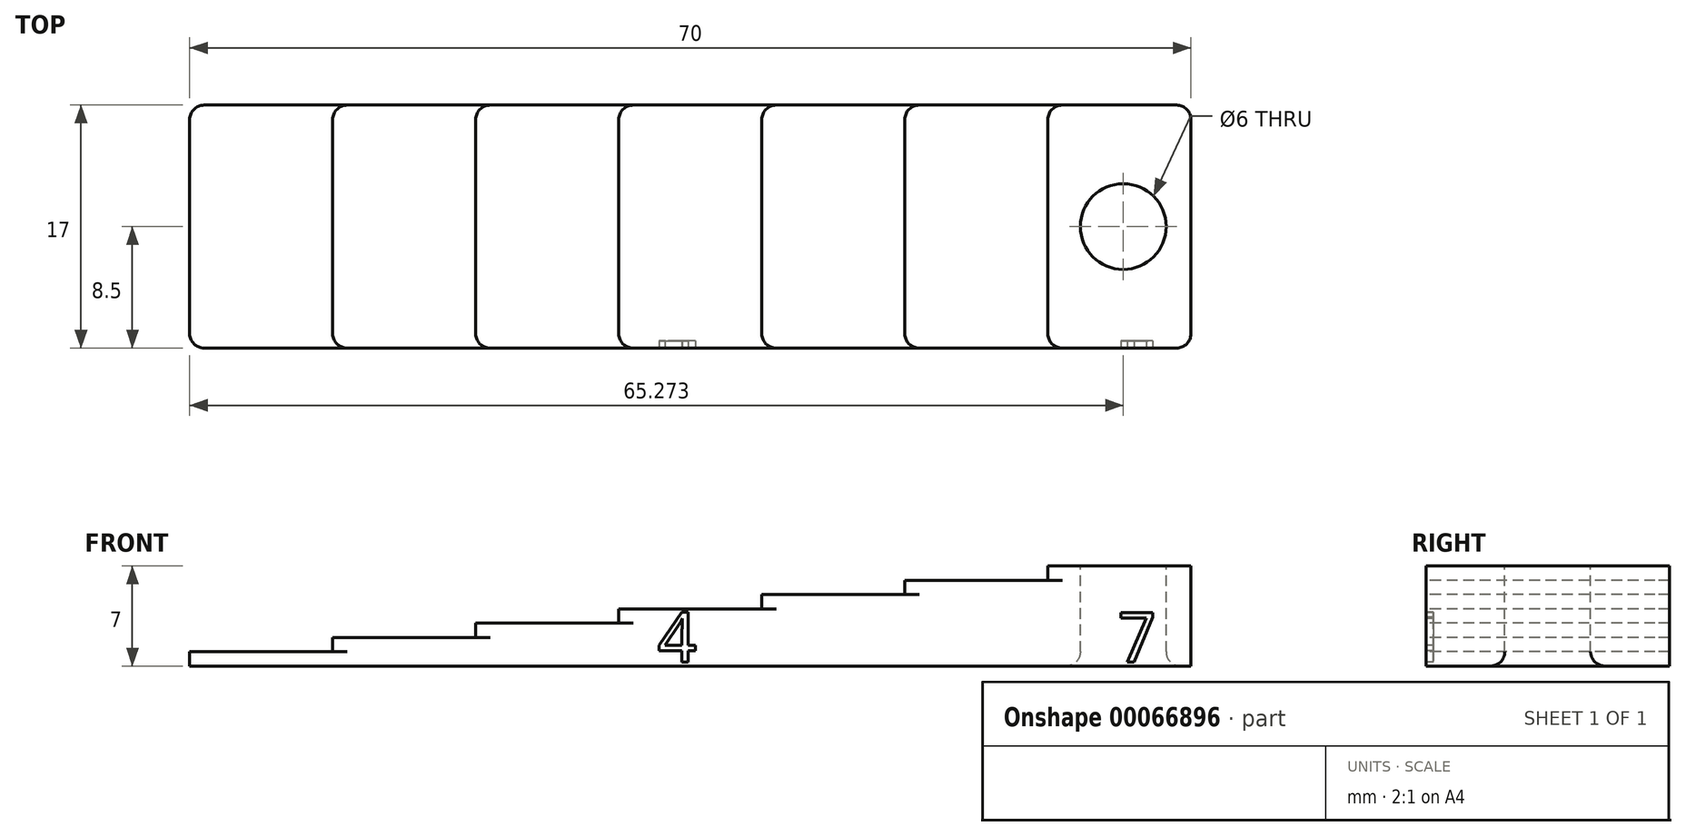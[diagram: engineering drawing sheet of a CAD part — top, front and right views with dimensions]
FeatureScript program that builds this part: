
annotation { "Feature Type Name" : "Feature", "Feature Type Description" : "" }
export const myFeature = defineFeature(function(context is Context, id is Id, definition is map)
    precondition{}
    {
        {
            var Q0;
            Q0=qCreatedBy(makeId("Top.planeOp"),FACE);
            var sketch = newSketch(context, id + "F0", { "sketchPlane" : qUnion([Q0])});
            skLineSegment(sketch, "E0.rect.bottom", {"start": v(35, 8.5) * mm, "end": v(-35, 8.5) * mm});
            skLineSegment(sketch, "E0.rect.top", {"start": v(35, -8.5) * mm, "end": v(-35, -8.5) * mm});
            skLineSegment(sketch, "E0.rect.left", {"start": v(35, 8.5) * mm, "end": v(35, -8.5) * mm});
            skLineSegment(sketch, "E0.rect.right", {"start": v(-35, 8.5) * mm, "end": v(-35, -8.5) * mm});
            skPoint(sketch, "E0.rect.middle", {"position": v(0, 0) * mm});
            skLineSegment(sketch, "E1.1.0.0", {"start": v(-25, 8.5) * mm, "end": v(-25, -8.5) * mm});
            skLineSegment(sketch, "E1.2.0.0", {"start": v(-15, 8.5) * mm, "end": v(-15, -8.5) * mm});
            skLineSegment(sketch, "E1.3.0.0", {"start": v(-5, 8.5) * mm, "end": v(-5, -8.5) * mm});
            skLineSegment(sketch, "E1.4.0.0", {"start": v(5, 8.5) * mm, "end": v(5, -8.5) * mm});
            skLineSegment(sketch, "E1.5.0.0", {"start": v(15, 8.5) * mm, "end": v(15, -8.5) * mm});
            skLineSegment(sketch, "E1.6.0.0", {"start": v(25, 8.5) * mm, "end": v(25, -8.5) * mm});
            skLineSegment(sketch, "E1.direction1", {"start": v(-35, -8.5) * mm, "end": v(-25, -8.5) * mm, "construction": true});
            skSolve(sketch);
        }
        {
            var Q0;
            {var subQ0=sQuery(id+"F0.wireOp",EDGE,"E0.rect.right");Q0=makeQuery(id+"F0.imprint","IMPRINT",FACE,{"disambiguationData":[TD([[makeQuery(id+"F0.imprint","IMPRINT",EDGE,{"derivedFrom":subQ0}),1.0]])]});}
            extrude(context, id + "F1", {"entities" : qUnion([Q0]), "depth" : 1 * mm});
        }
        {
            var Q0;
            {var subQ0=sQuery(id+"F0.wireOp",EDGE,"E1.1.0.0");Q0=makeQuery(id+"F0.imprint","IMPRINT",FACE,{"disambiguationData":[TD([[makeQuery(id+"F0.imprint","IMPRINT",EDGE,{"derivedFrom":subQ0}),1.0]])]});}
            extrude(context, id + "F2", {"entities" : qUnion([Q0]), "operationType" : NewBodyOperationType.ADD, "depth" : 2 * mm});
        }
        {
            var Q0;
            {var subQ0=sQuery(id+"F0.wireOp",EDGE,"E1.2.0.0");Q0=makeQuery(id+"F0.imprint","IMPRINT",FACE,{"disambiguationData":[TD([[makeQuery(id+"F0.imprint","IMPRINT",EDGE,{"derivedFrom":subQ0}),1.0]])]});}
            extrude(context, id + "F3", {"entities" : qUnion([Q0]), "operationType" : NewBodyOperationType.ADD, "depth" : 3 * mm});
        }
        {
            var Q0;
            {var subQ0=sQuery(id+"F0.wireOp",EDGE,"E1.3.0.0");Q0=makeQuery(id+"F0.imprint","IMPRINT",FACE,{"disambiguationData":[TD([[makeQuery(id+"F0.imprint","IMPRINT",EDGE,{"derivedFrom":subQ0}),1.0]])]});}
            extrude(context, id + "F4", {"entities" : qUnion([Q0]), "operationType" : NewBodyOperationType.ADD, "depth" : 4 * mm});
        }
        {
            var Q0;
            {var subQ0=sQuery(id+"F0.wireOp",EDGE,"E1.4.0.0");Q0=makeQuery(id+"F0.imprint","IMPRINT",FACE,{"disambiguationData":[TD([[makeQuery(id+"F0.imprint","IMPRINT",EDGE,{"derivedFrom":subQ0}),1.0]])]});}
            extrude(context, id + "F5", {"entities" : qUnion([Q0]), "operationType" : NewBodyOperationType.ADD, "depth" : 5 * mm});
        }
        {
            var Q0;
            {var subQ0=sQuery(id+"F0.wireOp",EDGE,"E1.5.0.0");Q0=makeQuery(id+"F0.imprint","IMPRINT",FACE,{"disambiguationData":[TD([[makeQuery(id+"F0.imprint","IMPRINT",EDGE,{"derivedFrom":subQ0}),1.0]])]});}
            extrude(context, id + "F6", {"entities" : qUnion([Q0]), "operationType" : NewBodyOperationType.ADD, "depth" : 6 * mm});
        }
        {
            var Q0;
            {var subQ0=sQuery(id+"F0.wireOp",EDGE,"E0.rect.left");Q0=makeQuery(id+"F0.imprint","IMPRINT",FACE,{"disambiguationData":[TD([[makeQuery(id+"F0.imprint","IMPRINT",EDGE,{"derivedFrom":subQ0}),-1.0]])]});}
            extrude(context, id + "F7", {"entities" : qUnion([Q0]), "operationType" : NewBodyOperationType.ADD, "depth" : 7 * mm});
        }
        {
            var Q0;
            {var subQ0=sQuery(id+"F0.wireOp",EDGE,"E0.rect.top");Q0=makeQuery(id+"F7.boolean.opBoolean","MERGE",FACE,{"derivedFrom":[makeQuery(id+"F6.boolean.opBoolean","MERGE",FACE,{"derivedFrom":[makeQuery(id+"F5.boolean.opBoolean","MERGE",FACE,{"derivedFrom":[makeQuery(id+"F4.boolean.opBoolean","MERGE",FACE,{"derivedFrom":[makeQuery(id+"F3.boolean.opBoolean","MERGE",FACE,{"derivedFrom":[makeQuery(id+"F2.boolean.opBoolean","MERGE",FACE,{"derivedFrom":[makeQuery(id+"F1.opExtrude","SWEPT_FACE",FACE,{"disambiguationData":[OSD([subQ0])]}),makeQuery(id+"F2.opExtrude","SWEPT_FACE",FACE,{"disambiguationData":[OSD([subQ0])]})]}),makeQuery(id+"F3.opExtrude","SWEPT_FACE",FACE,{"disambiguationData":[OSD([subQ0])]})]}),makeQuery(id+"F4.opExtrude","SWEPT_FACE",FACE,{"disambiguationData":[OSD([subQ0])]})]}),makeQuery(id+"F5.opExtrude","SWEPT_FACE",FACE,{"disambiguationData":[OSD([subQ0])]})]}),makeQuery(id+"F6.opExtrude","SWEPT_FACE",FACE,{"disambiguationData":[OSD([subQ0])]})]}),makeQuery(id+"F7.opExtrude","SWEPT_FACE",FACE,{"disambiguationData":[OSD([subQ0])]})]});}
            var sketch = newSketch(context, id + "F8", { "sketchPlane" : qUnion([Q0])});
            skText(sketch, "E2", { "text": "4          7", "fontName": "DroidSansMono.ttf"});
            const initialGuessF8  = {"E2": [-0.00233, 0.00028, 1, 0, 0.0035]};
            skSetInitialGuess(sketch, initialGuessF8);
            skSolve(sketch);
        }
        {
            var Q0;
            Q0 = qSketchRegion(id + "F8", true);
            extrude(context, id + "F9", {"entities" : qUnion([Q0]), "operationType" : NewBodyOperationType.REMOVE, "oppositeDirection" : true, "depth" : 0.5 * mm});
        }
        {
            var Q0;
            Q0=makeQuery(id+"F7.opExtrude","CAP_FACE",FACE,{"disambiguationData":[OSD([sQuery(id+"F0.wireOp",EDGE,"E0.rect.bottom"),sQuery(id+"F0.wireOp",EDGE,"E0.rect.top"),sQuery(id+"F0.wireOp",EDGE,"E0.rect.left"),sQuery(id+"F0.wireOp",EDGE,"E1.6.0.0")])],"isStart":false});
            var sketch = newSketch(context, id + "F10", { "sketchPlane" : qUnion([Q0])});
            skCircle(sketch, "E3", {"center": v(30.27, 0) * mm, "radius": 3 * mm});
            skSolve(sketch);
        }
        {
            var Q0;
            Q0 = qSketchRegion(id + "F10", true);
            extrude(context, id + "F11", {"entities" : qUnion([Q0]), "operationType" : NewBodyOperationType.REMOVE, "oppositeDirection" : true, "depth" : 25 * mm});
        }
        {
            var Q0;
            Q0=makeQuery(id+"F7.opExtrude","SWEPT_EDGE",EDGE,{"disambiguationData":[OSD([sQuery(id+"F0.wireOp",EDGE,"E0.rect.bottom"),sQuery(id+"F0.wireOp",EDGE,"E0.rect.left")])]});
            var Q1;
            Q1=makeQuery(id+"F7.opExtrude","SWEPT_EDGE",EDGE,{"disambiguationData":[OSD([sQuery(id+"F0.wireOp",EDGE,"E0.rect.top"),sQuery(id+"F0.wireOp",EDGE,"E0.rect.left")])]});
            var Q2;
            Q2=makeQuery(id+"F1.opExtrude","SWEPT_EDGE",EDGE,{"disambiguationData":[OSD([sQuery(id+"F0.wireOp",EDGE,"E0.rect.bottom"),sQuery(id+"F0.wireOp",EDGE,"E0.rect.right")])]});
            var Q3;
            Q3=makeQuery(id+"F1.opExtrude","SWEPT_EDGE",EDGE,{"disambiguationData":[OSD([sQuery(id+"F0.wireOp",EDGE,"E0.rect.top"),sQuery(id+"F0.wireOp",EDGE,"E0.rect.right")])]});
            var Q4;
            Q4=makeQuery(id+"F2.opExtrude","SWEPT_EDGE",EDGE,{"disambiguationData":[OSD([sQuery(id+"F0.wireOp",EDGE,"E0.rect.top"),sQuery(id+"F0.wireOp",EDGE,"E1.1.0.0")])]});
            var Q5;
            Q5=makeQuery(id+"F3.opExtrude","SWEPT_EDGE",EDGE,{"disambiguationData":[OSD([sQuery(id+"F0.wireOp",EDGE,"E0.rect.top"),sQuery(id+"F0.wireOp",EDGE,"E1.2.0.0")])]});
            var Q6;
            Q6=makeQuery(id+"F4.opExtrude","SWEPT_EDGE",EDGE,{"disambiguationData":[OSD([sQuery(id+"F0.wireOp",EDGE,"E0.rect.top"),sQuery(id+"F0.wireOp",EDGE,"E1.3.0.0")])]});
            var Q7;
            Q7=makeQuery(id+"F5.opExtrude","SWEPT_EDGE",EDGE,{"disambiguationData":[OSD([sQuery(id+"F0.wireOp",EDGE,"E0.rect.top"),sQuery(id+"F0.wireOp",EDGE,"E1.4.0.0")])]});
            var Q8;
            Q8=makeQuery(id+"F6.opExtrude","SWEPT_EDGE",EDGE,{"disambiguationData":[OSD([sQuery(id+"F0.wireOp",EDGE,"E0.rect.top"),sQuery(id+"F0.wireOp",EDGE,"E1.5.0.0")])]});
            var Q9;
            Q9=makeQuery(id+"F7.opExtrude","SWEPT_EDGE",EDGE,{"disambiguationData":[OSD([sQuery(id+"F0.wireOp",EDGE,"E0.rect.top"),sQuery(id+"F0.wireOp",EDGE,"E1.6.0.0")])]});
            var Q10;
            Q10=makeQuery(id+"F7.opExtrude","SWEPT_EDGE",EDGE,{"disambiguationData":[OSD([sQuery(id+"F0.wireOp",EDGE,"E0.rect.bottom"),sQuery(id+"F0.wireOp",EDGE,"E1.6.0.0")])]});
            var Q11;
            Q11=makeQuery(id+"F6.opExtrude","SWEPT_EDGE",EDGE,{"disambiguationData":[OSD([sQuery(id+"F0.wireOp",EDGE,"E0.rect.bottom"),sQuery(id+"F0.wireOp",EDGE,"E1.5.0.0")])]});
            var Q12;
            Q12=makeQuery(id+"F5.opExtrude","SWEPT_EDGE",EDGE,{"disambiguationData":[OSD([sQuery(id+"F0.wireOp",EDGE,"E0.rect.bottom"),sQuery(id+"F0.wireOp",EDGE,"E1.4.0.0")])]});
            var Q13;
            Q13=makeQuery(id+"F4.opExtrude","SWEPT_EDGE",EDGE,{"disambiguationData":[OSD([sQuery(id+"F0.wireOp",EDGE,"E0.rect.bottom"),sQuery(id+"F0.wireOp",EDGE,"E1.3.0.0")])]});
            var Q14;
            Q14=makeQuery(id+"F3.opExtrude","SWEPT_EDGE",EDGE,{"disambiguationData":[OSD([sQuery(id+"F0.wireOp",EDGE,"E0.rect.bottom"),sQuery(id+"F0.wireOp",EDGE,"E1.2.0.0")])]});
            var Q15;
            Q15=makeQuery(id+"F2.opExtrude","SWEPT_EDGE",EDGE,{"disambiguationData":[OSD([sQuery(id+"F0.wireOp",EDGE,"E0.rect.bottom"),sQuery(id+"F0.wireOp",EDGE,"E1.1.0.0")])]});
            var Q16;
            Q16=makeQuery(id+"F11.boolean.opBoolean","COPY",EDGE,{"derivedFrom":makeQuery(id+"F11.opExtrude","CAP_EDGE",EDGE,{"disambiguationData":[OSD([sQuery(id+"F10.wireOp",EDGE,"E3")])],"isStart":true})});
            var Q17;
            {var subQ0=sQuery(id+"F0.wireOp",EDGE,"E1.6.0.0");var subQ1=sQuery(id+"F0.wireOp",EDGE,"E0.rect.top");var subQ2=sQuery(id+"F0.wireOp",EDGE,"E0.rect.bottom");var subQ3=sQuery(id+"F0.wireOp",EDGE,"E1.5.0.0");var subQ4=sQuery(id+"F0.wireOp",EDGE,"E1.4.0.0");var subQ5=sQuery(id+"F0.wireOp",EDGE,"E1.3.0.0");var subQ6=sQuery(id+"F0.wireOp",EDGE,"E1.2.0.0");var subQ7=sQuery(id+"F0.wireOp",EDGE,"E1.1.0.0");Q17=makeQuery(id+"F11.boolean.opBoolean","INTERSECT",EDGE,{"derivedFrom":[makeQuery(id+"F7.boolean.opBoolean","MERGE",FACE,{"derivedFrom":[makeQuery(id+"F6.boolean.opBoolean","MERGE",FACE,{"derivedFrom":[makeQuery(id+"F5.boolean.opBoolean","MERGE",FACE,{"derivedFrom":[makeQuery(id+"F4.boolean.opBoolean","MERGE",FACE,{"derivedFrom":[makeQuery(id+"F3.boolean.opBoolean","MERGE",FACE,{"derivedFrom":[makeQuery(id+"F2.boolean.opBoolean","MERGE",FACE,{"derivedFrom":[makeQuery(id+"F1.opExtrude","CAP_FACE",FACE,{"disambiguationData":[OSD([subQ2,subQ1,sQuery(id+"F0.wireOp",EDGE,"E0.rect.right"),subQ7])],"isStart":true}),makeQuery(id+"F2.opExtrude","CAP_FACE",FACE,{"disambiguationData":[OSD([subQ2,subQ1,subQ7,subQ6])],"isStart":true})]}),makeQuery(id+"F3.opExtrude","CAP_FACE",FACE,{"disambiguationData":[OSD([subQ2,subQ1,subQ6,subQ5])],"isStart":true})]}),makeQuery(id+"F4.opExtrude","CAP_FACE",FACE,{"disambiguationData":[OSD([subQ2,subQ1,subQ5,subQ4])],"isStart":true})]}),makeQuery(id+"F5.opExtrude","CAP_FACE",FACE,{"disambiguationData":[OSD([subQ2,subQ1,subQ4,subQ3])],"isStart":true})]}),makeQuery(id+"F6.opExtrude","CAP_FACE",FACE,{"disambiguationData":[OSD([subQ2,subQ1,subQ3,subQ0])],"isStart":true})]}),makeQuery(id+"F7.opExtrude","CAP_FACE",FACE,{"disambiguationData":[OSD([subQ2,subQ1,sQuery(id+"F0.wireOp",EDGE,"E0.rect.left"),subQ0])],"isStart":true})]}),makeQuery(id+"F11.opExtrude","SWEPT_FACE",FACE,{"disambiguationData":[OSD([sQuery(id+"F10.wireOp",EDGE,"E3")])]})]});}
            fillet(context, id + "F12", {"entities" : qUnion([Q0, Q1, Q2, Q3, Q4, Q5, Q6, Q7, Q8, Q9, Q10, Q11, Q12, Q13, Q14, Q15, Q16, Q17]), "radius" : 1 * mm, "tangentPropagation" : true, "allowEdgeOverflow" : false});
        }
    });
